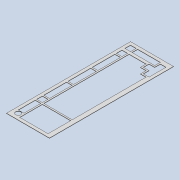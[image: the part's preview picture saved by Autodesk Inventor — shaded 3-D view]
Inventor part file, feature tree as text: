
AUTODESK INVENTOR PART (.ipt)
format: ipt  version: 2021 (Build 250183000, 183)  size: 449,536 bytes
history: native  units: mm
features: extrude x1, sketch x1
ambient origin geometry x8: Origin, YZ Plane, XZ Plane, XY Plane, X Axis, Y Axis, Z Axis, Center Point
bodies: Solid1 (feature_tree)
feature tree (2):
  extrude  "Extrusion1"  Depth=1.0mm
  sketch  "Sketch1"  dims[d0=37.05mm d1=18.0mm d2=0.0mm d3=0.0mm d4=18.0mm d5=1.05mm d6=37.05mm d7=18.0mm d8=1.05mm d10=18.0mm d12=18.0mm d13=18.0mm d15=18.0mm d16=18.0mm d17=1.05mm d18=1.05mm d21=18.0mm d25=1.05mm d26=37.05mm d27=18.0mm d33=1.05mm d34=18.0mm d37=22.7625mm d38=5.8125mm d39=22.7625mm d40=22.7625mm d41=1.05mm d42=1.05mm d43=1.05mm d44=1.05mm d45=1.05mm d46=1.05mm d47=18.0mm d48=18.0mm d49=18.0mm d50=118.0mm d51=41.8125mm d52=1.05mm d53=32.2875mm d54=27.525mm d55=18.0mm d56=1.05mm d57=1.05mm d58=1.05mm d59=1.05mm d60=1.05mm d61=1.05mm d62=1.05mm d63=1.05mm d64=1.05mm d66=18.0mm d67=18.0mm d68=18.0mm d69=18.0mm d70=18.0mm d71=18.0mm d72=18.0mm d73=18.0mm d74=18.0mm d75=18.0mm d76=1.05mm d77=1.05mm d78=32.2875mm d79=18.0mm d80=18.0mm d81=1.05mm d82=1.05mm d83=1.05mm d84=1.05mm d85=1.05mm d86=18.0mm d87=18.0mm d88=18.0mm d89=1.05mm d90=1.05mm d91=1.05mm d92=1.05mm d93=1.05mm d94=1.05mm d95=1.05mm d96=18.0mm d97=18.0mm d98=18.0mm d99=18.0mm d100=18.0mm d101=18.0mm d102=41.8125mm d103=1.05mm d104=1.05mm d105=1.05mm d106=1.05mm d107=1.05mm d108=1.05mm d109=1.05mm d110=1.05mm d111=1.05mm d112=1.05mm d116=18.0mm d117=18.0mm d118=18.0mm d119=18.0mm d120=18.0mm d121=18.0mm d122=18.0mm d123=18.0mm d124=18.0mm d125=18.0mm d127=18.0mm d128=18.0mm d129=1.05mm d130=1.05mm d131=27.525mm d132=1.05mm d133=18.0mm d134=18.0mm d135=18.0mm d136=1.05mm d137=1.05mm d138=1.05mm d139=1.05mm d140=1.05mm d141=1.05mm d142=1.05mm d143=1.05mm d144=1.05mm d145=1.05mm d146=1.05mm d147=1.05mm d148=1.05mm d149=37.05mm d150=18.0mm d151=18.0mm d152=18.0mm d153=18.0mm d154=18.0mm d155=18.0mm d156=18.0mm d157=18.0mm d158=18.0mm d159=1.05mm d160=1.05mm d161=1.05mm d162=1.05mm d163=1.05mm d164=1.05mm d165=5.8125mm d166=5.8125mm d168=5.8125mm d169=5.8125mm d170=18.0mm d171=18.0mm d172=18.0mm d173=1.05mm d174=1.05mm d176=1.05mm d178=1.05mm d179=1.05mm d180=1.05mm d181=1.05mm d182=1.05mm d183=18.0mm d184=18.0mm d185=18.0mm d186=18.0mm d187=18.0mm d188=18.0mm d189=18.0mm d191=18.0mm d192=18.0mm d193=18.0mm d194=5.8125mm d195=1.05mm d196=5.8125mm d197=18.0mm d198=18.0mm d199=18.0mm d200=18.0mm d201=18.0mm d202=18.0mm d203=18.0mm d204=1.05mm d205=1.05mm d206=1.05mm d207=18.0mm d208=18.0mm d209=18.0mm d210=18.0mm d211=1.05mm d212=18.0mm d213=18.0mm d214=1.05mm d215=1.05mm d216=18.0mm d218=5.8125mm d219=5.8125mm d220=5.8125mm d221=5.8125mm d223=17.0mm d224=17.5mm d225=0.5mm d226=0.5mm d227=0.5mm d228=0.5mm d229=0.5mm d230=0.5mm d231=0.5mm d232=0.5mm d233=0.5mm d234=0.5mm d235=0.5mm d236=0.5mm d237=0.5mm d238=0.5mm d239=0.5mm d240=0.5mm d241=0.5mm d242=0.5mm d243=0.5mm d244=0.5mm d245=0.5mm d246=0.5mm d247=0.5mm d248=0.5mm d249=0.5mm d250=0.5mm d251=0.5mm d253=0.5mm d254=0.5mm d255=0.5mm d256=0.5mm d257=0.5mm d258=0.5mm d259=0.5mm d260=0.5mm d261=0.5mm d262=0.5mm d263=0.5mm d264=10.05mm d265=14.8125mm d266=10.0mm d267=10.0mm d268=10.0mm d269=10.0mm d270=1.0mm d271=0.0mm]
